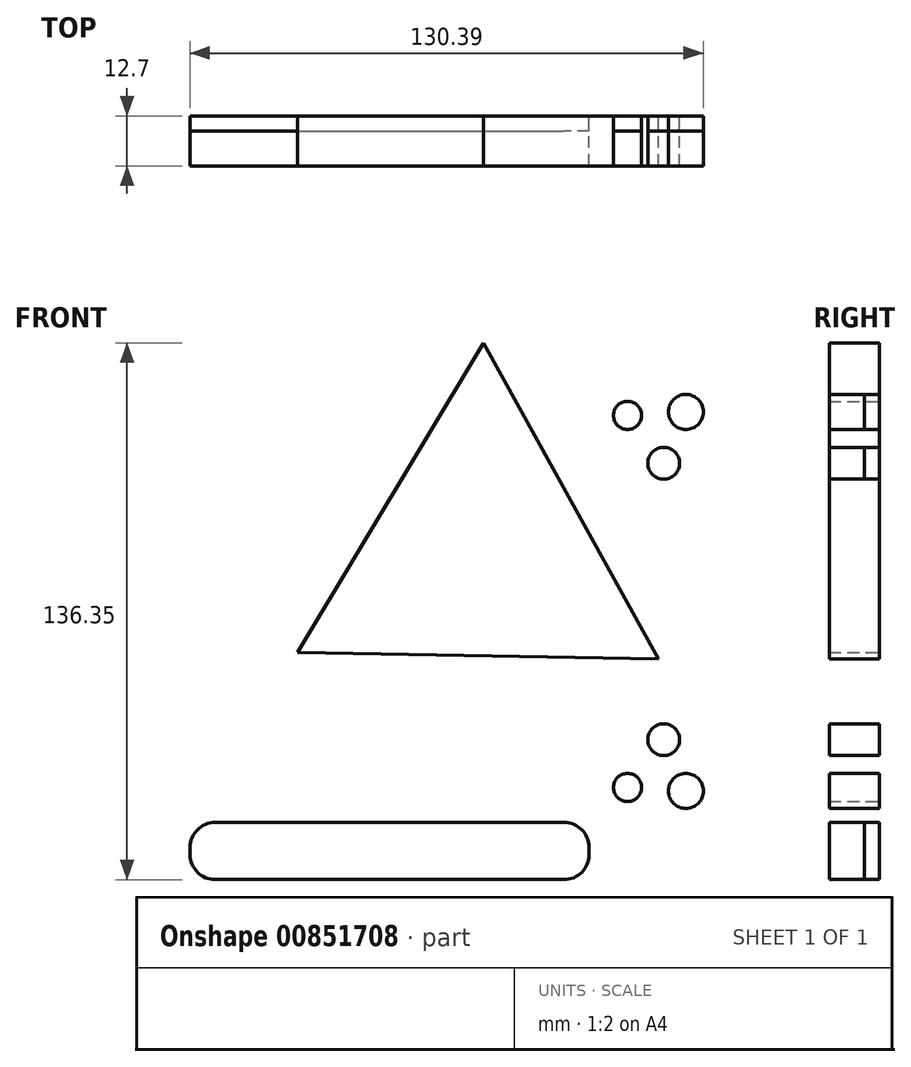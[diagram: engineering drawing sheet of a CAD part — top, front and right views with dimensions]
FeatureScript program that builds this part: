
annotation { "Feature Type Name" : "Feature", "Feature Type Description" : "" }
export const myFeature = defineFeature(function(context is Context, id is Id, definition is map)
    precondition{}
    {
        {
            var Q0;
            Q0=qCreatedBy(makeId("Front.planeOp"),FACE);
            var sketch = newSketch(context, id + "F0", { "sketchPlane" : qUnion([Q0])});
            skLineSegment(sketch, "E0.0", {"start": v(44.5, -14.56) * mm, "end": v(-47.25, -13) * mm});
            skLineSegment(sketch, "E0.1", {"start": v(-47.25, -13) * mm, "end": v(-0.03, 65.67) * mm});
            skLineSegment(sketch, "E0.2", {"start": v(-0.03, 65.67) * mm, "end": v(44.5, -14.56) * mm});
            skPoint(sketch, "E0.0.midPoint", {"position": v(-1.37, -13.78) * mm});
            skSolve(sketch);
        }
        {
            var Q0;
            Q0=makeQuery(id+"F0.imprint","IMPRINT",FACE,{"disambiguationData":[TD([[makeQuery(id+"F0.imprint","IMPRINT",EDGE,{"derivedFrom":sQuery(id+"F0.wireOp",EDGE,"E0.0")}),-1.0]])]});
            extrude(context, id + "F1", {"entities" : qUnion([Q0]), "depth" : 12.7 * mm, "offsetDistance" : 25.4 * mm});
        }
        {
            var Q0;
            Q0=qCreatedBy(makeId("Front.planeOp"),FACE);
            var sketch = newSketch(context, id + "F2", { "sketchPlane" : qUnion([Q0])});
            skLineSegment(sketch, "E1.bottom", {"start": v(-68.18, -56.16) * mm, "end": v(20.47, -56.16) * mm});
            skLineSegment(sketch, "E1.top", {"start": v(-68.18, -70.68) * mm, "end": v(20.47, -70.68) * mm});
            skLineSegment(sketch, "E1.left", {"start": v(-74.53, -62.5) * mm, "end": v(-74.53, -64.33) * mm});
            skLineSegment(sketch, "E1.right", {"start": v(26.82, -62.5) * mm, "end": v(26.82, -64.33) * mm});
            skPoint(sketch, "E2.visualSharp", {"position": v(-74.53, -56.16) * mm});
            skArc(sketch, "E2.filletArc", {"start": v(-68.18, -56.16) * mm, "mid": v(-72.67, -58.02) * mm, "end": v(-74.53, -62.5) * mm});
            skPoint(sketch, "E3.visualSharp", {"position": v(26.82, -56.16) * mm});
            skArc(sketch, "E3.filletArc", {"start": v(26.82, -62.5) * mm, "mid": v(24.96, -58.02) * mm, "end": v(20.47, -56.16) * mm});
            skPoint(sketch, "E4.visualSharp", {"position": v(26.82, -70.68) * mm});
            skArc(sketch, "E4.filletArc", {"start": v(20.47, -70.68) * mm, "mid": v(24.96, -68.82) * mm, "end": v(26.82, -64.33) * mm});
            skPoint(sketch, "E5.visualSharp", {"position": v(-74.53, -70.68) * mm});
            skArc(sketch, "E5.filletArc", {"start": v(-74.53, -64.33) * mm, "mid": v(-72.67, -68.82) * mm, "end": v(-68.18, -70.68) * mm});
            skCircle(sketch, "E6", {"center": v(36.6, 47.27) * mm, "radius": 3.57 * mm});
            skCircle(sketch, "E7", {"center": v(45.78, 35.12) * mm, "radius": 4.03 * mm});
            skCircle(sketch, "E8", {"center": v(51.41, 48.15) * mm, "radius": 4.45 * mm});
            skSolve(sketch);
        }
        {
            var Q0;
            Q0 = qSketchRegion(id + "F2", true);
            extrude(context, id + "F3", {"entities" : qUnion([Q0]), "depth" : 12.7 * mm, "offsetDistance" : 25.4 * mm});
        }
        {
            var Q0;
            Q0 = qSketchRegion(id + "F2", true);
            extrude(context, id + "F4", {"entities" : qUnion([Q0]), "depth" : 3.8 * mm, "offsetDistance" : 25.4 * mm});
        }
        {
            var Q0;
            Q0=makeQuery(id+"F3.opExtrude","SWEPT_BODY",BODY,{"disambiguationData":[OSD([sQuery(id+"F2.wireOp",EDGE,"E8")])]});
            var Q1;
            Q1=makeQuery(id+"F3.opExtrude","SWEPT_BODY",BODY,{"disambiguationData":[OSD([sQuery(id+"F2.wireOp",EDGE,"E6")])]});
            var Q2;
            Q2=makeQuery(id+"F3.opExtrude","SWEPT_BODY",BODY,{"disambiguationData":[OSD([sQuery(id+"F2.wireOp",EDGE,"E7")])]});
            var Q3;
            Q3=qCreatedBy(makeId("Top.planeOp"),FACE);
            mirror(context, id + "F5", {"entities" : qUnion([Q0, Q1, Q2]), "mirrorPlane" : qUnion([Q3])});
        }
    });
